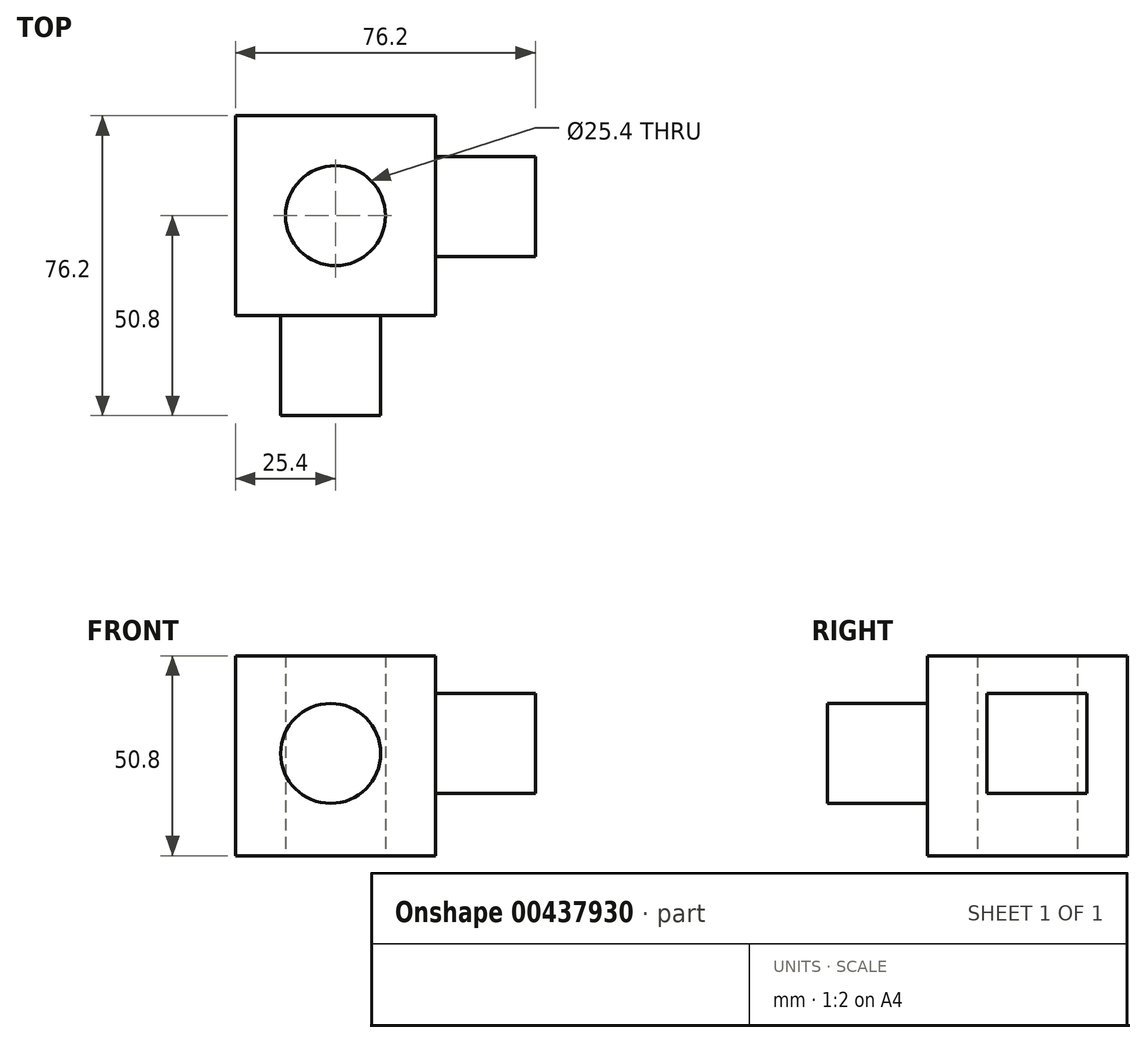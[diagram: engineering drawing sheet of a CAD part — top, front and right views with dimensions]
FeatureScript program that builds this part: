
annotation { "Feature Type Name" : "Feature", "Feature Type Description" : "" }
export const myFeature = defineFeature(function(context is Context, id is Id, definition is map)
    precondition{}
    {
        {
            var Q0;
            Q0=qCreatedBy(makeId("Front.planeOp"),FACE);
            var sketch = newSketch(context, id + "F0", { "sketchPlane" : qUnion([Q0])});
            skLineSegment(sketch, "E0.bottom", {"start": v(0, 0) * mm, "end": v(-50.8, 0) * mm});
            skLineSegment(sketch, "E0.top", {"start": v(0, 50.8) * mm, "end": v(-50.8, 50.8) * mm});
            skLineSegment(sketch, "E0.left", {"start": v(0, 0) * mm, "end": v(0, 50.8) * mm});
            skLineSegment(sketch, "E0.right", {"start": v(-50.8, 0) * mm, "end": v(-50.8, 50.8) * mm});
            skSolve(sketch);
        }
        {
            var Q0;
            Q0 = qSketchRegion(id + "F0", true);
            extrude(context, id + "F1", {"entities" : qUnion([Q0]), "depth" : 50.8 * mm});
        }
        {
            var Q0;
            Q0=qCreatedBy(makeId("Front.planeOp"),FACE);
            var sketch = newSketch(context, id + "F2", { "sketchPlane" : qUnion([Q0])});
            skCircle(sketch, "E1", {"center": v(-26.6, 26) * mm, "radius": 12.7 * mm});
            skSolve(sketch);
        }
        {
            var Q0;
            Q0 = qSketchRegion(id + "F2", true);
            extrude(context, id + "F3", {"entities" : qUnion([Q0]), "operationType" : NewBodyOperationType.ADD, "depth" : 76.2 * mm});
        }
        {
            var Q0;
            Q0=makeQuery(id+"F1.opExtrude","SWEPT_FACE",FACE,{"disambiguationData":[OSD([sQuery(id+"F0.wireOp",EDGE,"E0.left")])]});
            var sketch = newSketch(context, id + "F4", { "sketchPlane" : qUnion([Q0])});
            skLineSegment(sketch, "E2.bottom", {"start": v(-10.3, 41.28) * mm, "end": v(-35.7, 41.28) * mm});
            skLineSegment(sketch, "E2.top", {"start": v(-10.3, 15.88) * mm, "end": v(-35.7, 15.88) * mm});
            skLineSegment(sketch, "E2.left", {"start": v(-10.3, 41.28) * mm, "end": v(-10.3, 15.88) * mm});
            skLineSegment(sketch, "E2.right", {"start": v(-35.7, 41.28) * mm, "end": v(-35.7, 15.88) * mm});
            skSolve(sketch);
        }
        {
            var Q0;
            Q0=makeQuery(id+"F4.imprint","IMPRINT",FACE,{"disambiguationData":[TD([[makeQuery(id+"F4.imprint","IMPRINT",EDGE,{"derivedFrom":sQuery(id+"F4.wireOp",EDGE,"E2.bottom")}),1.0]])]});
            extrude(context, id + "F5", {"entities" : qUnion([Q0]), "operationType" : NewBodyOperationType.ADD, "depth" : 25.4 * mm});
        }
        {
            var Q0;
            Q0=makeQuery(id+"F1.opExtrude","SWEPT_FACE",FACE,{"disambiguationData":[OSD([sQuery(id+"F0.wireOp",EDGE,"E0.bottom")])]});
            var sketch = newSketch(context, id + "F6", { "sketchPlane" : qUnion([Q0])});
            skCircle(sketch, "E3", {"center": v(-25.4, 25.4) * mm, "radius": 12.7 * mm});
            skSolve(sketch);
        }
        {
            var Q0;
            Q0=makeQuery(id+"F6.imprint","IMPRINT",FACE,{"disambiguationData":[TD([[makeQuery(id+"F6.imprint","IMPRINT",EDGE,{"derivedFrom":sQuery(id+"F6.wireOp",EDGE,"E3")}),1.0]])]});
            extrude(context, id + "F7", {"entities" : qUnion([Q0]), "operationType" : NewBodyOperationType.REMOVE, "oppositeDirection" : true, "depth" : 50.8 * mm});
        }
    });
